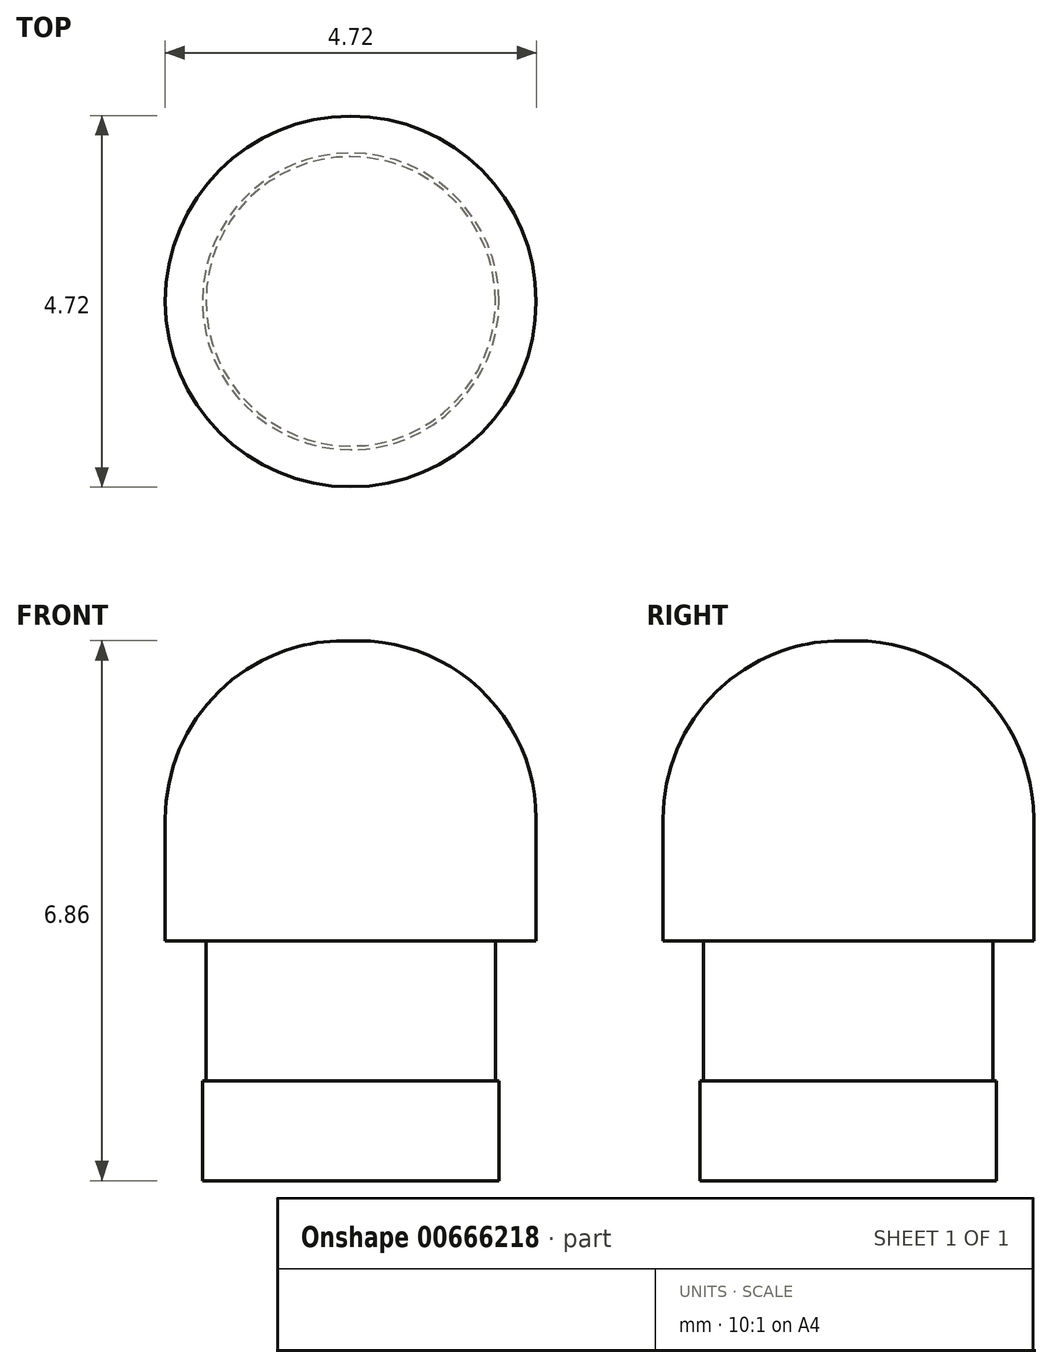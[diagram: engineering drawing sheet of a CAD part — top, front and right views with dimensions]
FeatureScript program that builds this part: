
annotation { "Feature Type Name" : "Feature", "Feature Type Description" : "" }
export const myFeature = defineFeature(function(context is Context, id is Id, definition is map)
    precondition{}
    {
        {
            var Q0;
            Q0=qCreatedBy(makeId("Top.planeOp"),FACE);
            var sketch = newSketch(context, id + "F0", { "sketchPlane" : qUnion([Q0])});
            skCircle(sketch, "E0", {"center": v(0, 0) * mm, "radius": 1.84 * mm});
            skSolve(sketch);
        }
        {
            var Q0;
            Q0=makeQuery(id+"F0.imprint","IMPRINT",FACE,{"disambiguationData":[TD([[makeQuery(id+"F0.imprint","IMPRINT",EDGE,{"derivedFrom":sQuery(id+"F0.wireOp",EDGE,"E0")}),1.0]])]});
            extrude(context, id + "F1", {"entities" : qUnion([Q0]), "depth" : 1.78 * mm, "offsetDistance" : 25.4 * mm});
        }
        {
            var Q0;
            Q0=makeQuery(id+"F1.opExtrude","CAP_FACE",FACE,{"disambiguationData":[OSD([sQuery(id+"F0.wireOp",EDGE,"E0")])],"isStart":false});
            var sketch = newSketch(context, id + "F2", { "sketchPlane" : qUnion([Q0])});
            skCircle(sketch, "E1", {"center": v(0, 0) * mm, "radius": 2.36 * mm});
            skSolve(sketch);
        }
        {
            var Q0;
            Q0=makeQuery(id+"F2.imprint","IMPRINT",FACE,{"disambiguationData":[TD([[makeQuery(id+"F2.imprint","IMPRINT",EDGE,{"derivedFrom":sQuery(id+"F2.wireOp",EDGE,"E1")}),1.0]])]});
            var Q1;
            Q1=makeQuery(id+"F2.imprint","IMPRINT",FACE,{"disambiguationData":[TD([[makeQuery(id+"F2.imprint","IMPRINT",EDGE,{"derivedFrom":makeQuery(id+"F1.opExtrude","CAP_EDGE",EDGE,{"disambiguationData":[OSD([sQuery(id+"F0.wireOp",EDGE,"E0")])],"isStart":false})}),1.0]])]});
            extrude(context, id + "F3", {"entities" : qUnion([Q0, Q1]), "depth" : 3.8 * mm, "offsetDistance" : 25.4 * mm});
        }
        {
            var Q0;
            Q0=makeQuery(id+"F3.opExtrude","CAP_FACE",FACE,{"disambiguationData":[OSD([sQuery(id+"F2.wireOp",EDGE,"E1")])],"isStart":false});
            fillet(context, id + "F4", {"entities" : qUnion([Q0]), "radius" : 2.26 * mm, "tangentPropagation" : true, "allowEdgeOverflow" : false});
        }
        {
            var Q0;
            Q0=makeQuery(id+"F1.opExtrude","CAP_FACE",FACE,{"disambiguationData":[OSD([sQuery(id+"F0.wireOp",EDGE,"E0")])],"isStart":true});
            var sketch = newSketch(context, id + "F5", { "sketchPlane" : qUnion([Q0])});
            skCircle(sketch, "E2", {"center": v(0, 0) * mm, "radius": 1.88 * mm});
            skSolve(sketch);
        }
        {
            var Q0;
            Q0=makeQuery(id+"F5.imprint","IMPRINT",FACE,{"disambiguationData":[TD([[makeQuery(id+"F5.imprint","IMPRINT",EDGE,{"derivedFrom":sQuery(id+"F5.wireOp",EDGE,"E2")}),1.0]])]});
            var Q1;
            Q1=makeQuery(id+"F5.imprint","IMPRINT",FACE,{"disambiguationData":[TD([[makeQuery(id+"F5.imprint","IMPRINT",EDGE,{"derivedFrom":makeQuery(id+"F1.opExtrude","CAP_EDGE",EDGE,{"disambiguationData":[OSD([sQuery(id+"F0.wireOp",EDGE,"E0")])],"isStart":true})}),-1.0]])]});
            var Q2;
            Q2=sQuery(id+"F5.wireOp",EDGE,"E2");
            extrude(context, id + "F6", {"entities" : qUnion([Q0, Q1]), "surfaceEntities" : qUnion([Q2]), "depth" : 1.27 * mm, "offsetDistance" : 25.4 * mm});
        }
    });
